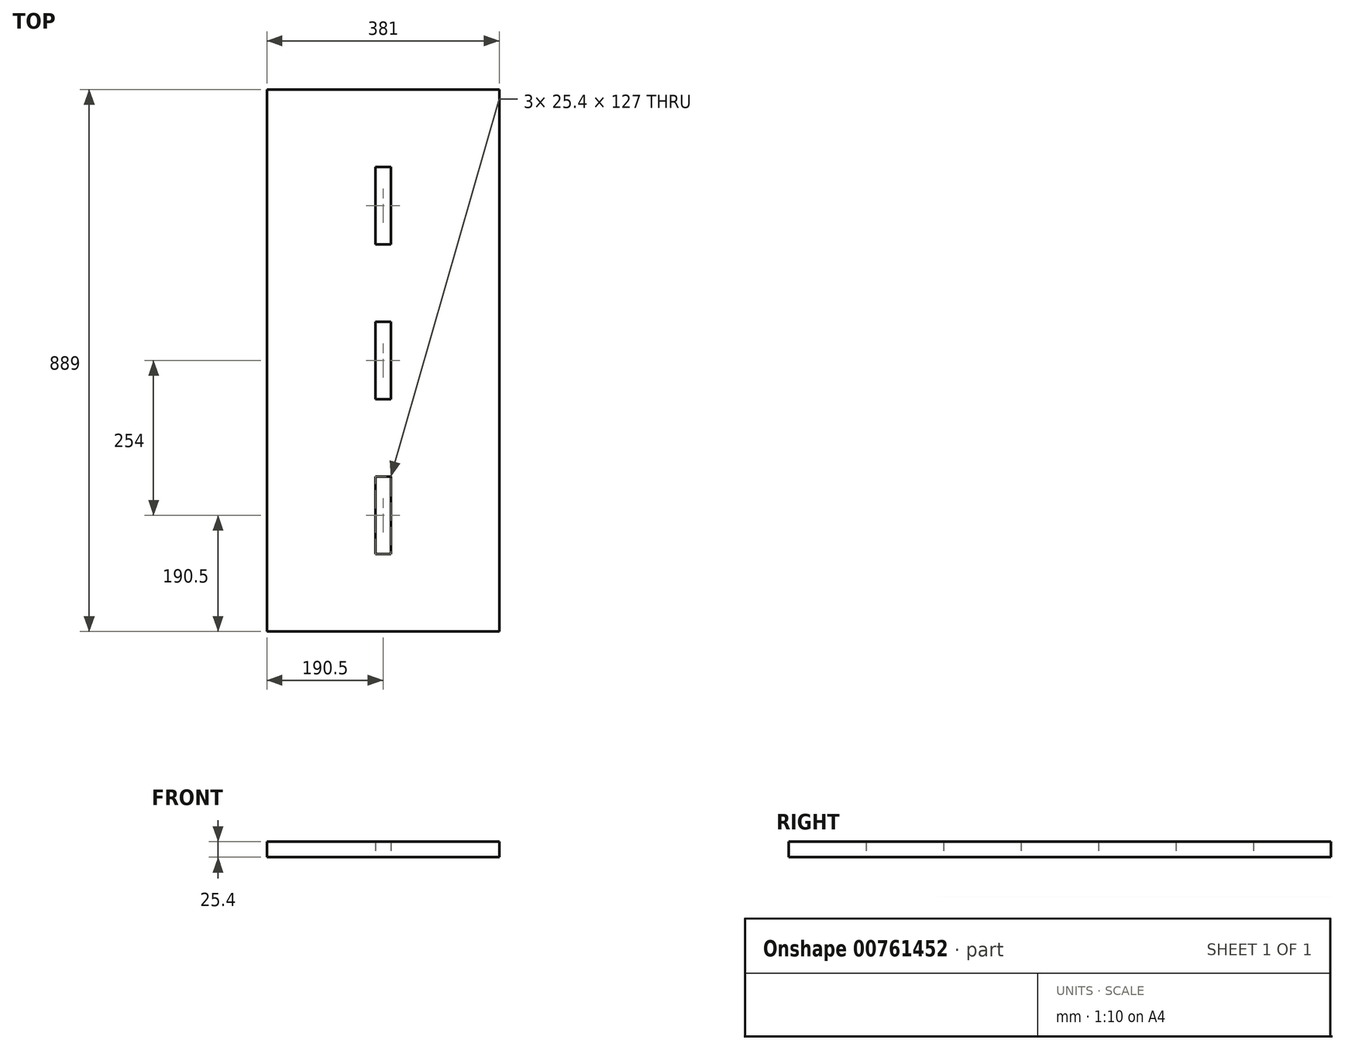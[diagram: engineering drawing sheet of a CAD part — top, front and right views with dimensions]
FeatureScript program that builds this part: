
annotation { "Feature Type Name" : "Feature", "Feature Type Description" : "" }
export const myFeature = defineFeature(function(context is Context, id is Id, definition is map)
    precondition{}
    {
        {
            var Q0;
            Q0=qCreatedBy(makeId("Top.planeOp"),FACE);
            var sketch = newSketch(context, id + "F0", { "sketchPlane" : qUnion([Q0])});
            skLineSegment(sketch, "E0.bottom", {"start": v(-190.5, 381) * mm, "end": v(190.5, 381) * mm});
            skLineSegment(sketch, "E0.top", {"start": v(-190.5, -381) * mm, "end": v(190.5, -381) * mm});
            skLineSegment(sketch, "E0.left", {"start": v(-190.5, 381) * mm, "end": v(-190.5, -381) * mm});
            skLineSegment(sketch, "E0.right", {"start": v(190.5, 381) * mm, "end": v(190.5, -381) * mm});
            skPoint(sketch, "E0.middle", {"position": v(0, 0) * mm});
            skLineSegment(sketch, "E1.bottom", {"start": v(-12.7, 381) * mm, "end": v(12.7, 381) * mm});
            skLineSegment(sketch, "E1.top", {"start": v(-12.7, -381) * mm, "end": v(12.7, -381) * mm});
            skLineSegment(sketch, "E1.left", {"start": v(-12.7, 381) * mm, "end": v(-12.7, -381) * mm});
            skLineSegment(sketch, "E1.right", {"start": v(12.7, 381) * mm, "end": v(12.7, -381) * mm});
            skLineSegment(sketch, "E2", {"start": v(-12.7, 254) * mm, "end": v(12.7, 254) * mm});
            skLineSegment(sketch, "E3", {"start": v(-12.7, 127) * mm, "end": v(12.7, 127) * mm});
            skLineSegment(sketch, "E4", {"start": v(-12.7, 0) * mm, "end": v(12.7, 0) * mm});
            skLineSegment(sketch, "E5", {"start": v(-12.7, -127) * mm, "end": v(12.7, -127) * mm});
            skLineSegment(sketch, "E6", {"start": v(-12.7, -254) * mm, "end": v(12.7, -254) * mm});
            skLineSegment(sketch, "E7.bottom", {"start": v(190.5, 381) * mm, "end": v(-190.5, 381) * mm});
            skLineSegment(sketch, "E7.top", {"start": v(190.5, 508) * mm, "end": v(-190.5, 508) * mm});
            skLineSegment(sketch, "E7.left", {"start": v(190.5, 381) * mm, "end": v(190.5, 508) * mm});
            skLineSegment(sketch, "E7.right", {"start": v(-190.5, 381) * mm, "end": v(-190.5, 508) * mm});
            skLineSegment(sketch, "E8.bottom", {"start": v(849.8, 508) * mm, "end": v(-849.8, 508) * mm});
            skLineSegment(sketch, "E9", {"start": v(-849.8, -381) * mm, "end": v(-190.5, -381) * mm});
            skLineSegment(sketch, "E10", {"start": v(190.5, -381) * mm, "end": v(849.8, -381) * mm});
            skLineSegment(sketch, "E11", {"start": v(849.8, 508) * mm, "end": v(849.8, -381) * mm});
            skLineSegment(sketch, "E12", {"start": v(-849.8, 508) * mm, "end": v(-849.8, -381) * mm});
            skCircle(sketch, "E13", {"center": v(-482.89, 357.76) * mm, "radius": 50.8 * mm});
            skCircle(sketch, "E14", {"center": v(514.14, 61.89) * mm, "radius": 50.8 * mm});
            skSolve(sketch);
        }
        {
            var Q0;
            {var subQ0=sQuery(id+"F0.wireOp",EDGE,"E0.left");Q0=makeQuery(id+"F0.imprint","IMPRINT",FACE,{"disambiguationData":[TD([[makeQuery(id+"F0.imprint","IMPRINT",EDGE,{"derivedFrom":subQ0}),1.0]])]});}
            var Q1;
            {var subQ0=sQuery(id+"F0.wireOp",EDGE,"E2");Q1=makeQuery(id+"F0.imprint","IMPRINT",FACE,{"disambiguationData":[TD([[makeQuery(id+"F0.imprint","IMPRINT",EDGE,{"derivedFrom":subQ0}),-1.0]])]});}
            var Q2;
            {var subQ0=sQuery(id+"F0.wireOp",EDGE,"E0.right");Q2=makeQuery(id+"F0.imprint","IMPRINT",FACE,{"disambiguationData":[TD([[makeQuery(id+"F0.imprint","IMPRINT",EDGE,{"derivedFrom":subQ0}),-1.0]])]});}
            var Q3;
            {var subQ0=sQuery(id+"F0.wireOp",EDGE,"E4");Q3=makeQuery(id+"F0.imprint","IMPRINT",FACE,{"disambiguationData":[TD([[makeQuery(id+"F0.imprint","IMPRINT",EDGE,{"derivedFrom":subQ0}),-1.0]])]});}
            var Q4;
            {var subQ3=sQuery(id+"F0.wireOp",EDGE,"E6");Q4=makeQuery(id+"F0.imprint","IMPRINT",FACE,{"disambiguationData":[TD([[makeQuery(id+"F0.imprint","IMPRINT",EDGE,{"derivedFrom":subQ3}),-1.0]])]});}
            var Q5;
            Q5=makeQuery(id+"F0.imprint","IMPRINT",FACE,{"disambiguationData":[TD([[makeQuery(id+"F0.imprint","IMPRINT",EDGE,{"derivedFrom":sQuery(id+"F0.wireOp",EDGE,"E7.top")}),1.0]])]});
            var Q6;
            {var subQ0=sQuery(id+"F0.wireOp",EDGE,"E7.left");Q6=makeQuery(id+"F0.imprint","IMPRINT",FACE,{"disambiguationData":[TD([[makeQuery(id+"F0.imprint","IMPRINT",EDGE,{"derivedFrom":subQ0}),1.0]])]});}
            extrude(context, id + "F1", {"entities" : qUnion([Q0, Q1, Q2, Q3, Q4, Q5, Q6]), "depth" : 25.4 * mm, "offsetDistance" : 25.4 * mm});
        }
        {
            var Q0;
            {var subQ0=sQuery(id+"F0.wireOp",EDGE,"E1.bottom");Q0=makeQuery(id+"F0.imprint","IMPRINT",FACE,{"disambiguationData":[TD([[makeQuery(id+"F0.imprint","IMPRINT",EDGE,{"derivedFrom":subQ0}),-1.0]])]});}
            var Q1;
            {var subQ0=sQuery(id+"F0.wireOp",EDGE,"E3");Q1=makeQuery(id+"F0.imprint","IMPRINT",FACE,{"disambiguationData":[TD([[makeQuery(id+"F0.imprint","IMPRINT",EDGE,{"derivedFrom":subQ0}),-1.0]])]});}
            var Q2;
            {var subQ0=sQuery(id+"F0.wireOp",EDGE,"E5");Q2=makeQuery(id+"F0.imprint","IMPRINT",FACE,{"disambiguationData":[TD([[makeQuery(id+"F0.imprint","IMPRINT",EDGE,{"derivedFrom":subQ0}),-1.0]])]});}
            var Q3;
            {var subQ3=sQuery(id+"F0.wireOp",EDGE,"E2");Q3=makeQuery(id+"F0.imprint","IMPRINT",FACE,{"disambiguationData":[TD([[makeQuery(id+"F0.imprint","IMPRINT",EDGE,{"derivedFrom":subQ3}),1.0]])]});}
            extrude(context, id + "F2", {"entities" : qUnion([Q0, Q1, Q2, Q3]), "depth" : 25.4 * mm, "offsetDistance" : 25.4 * mm});
        }
    });
